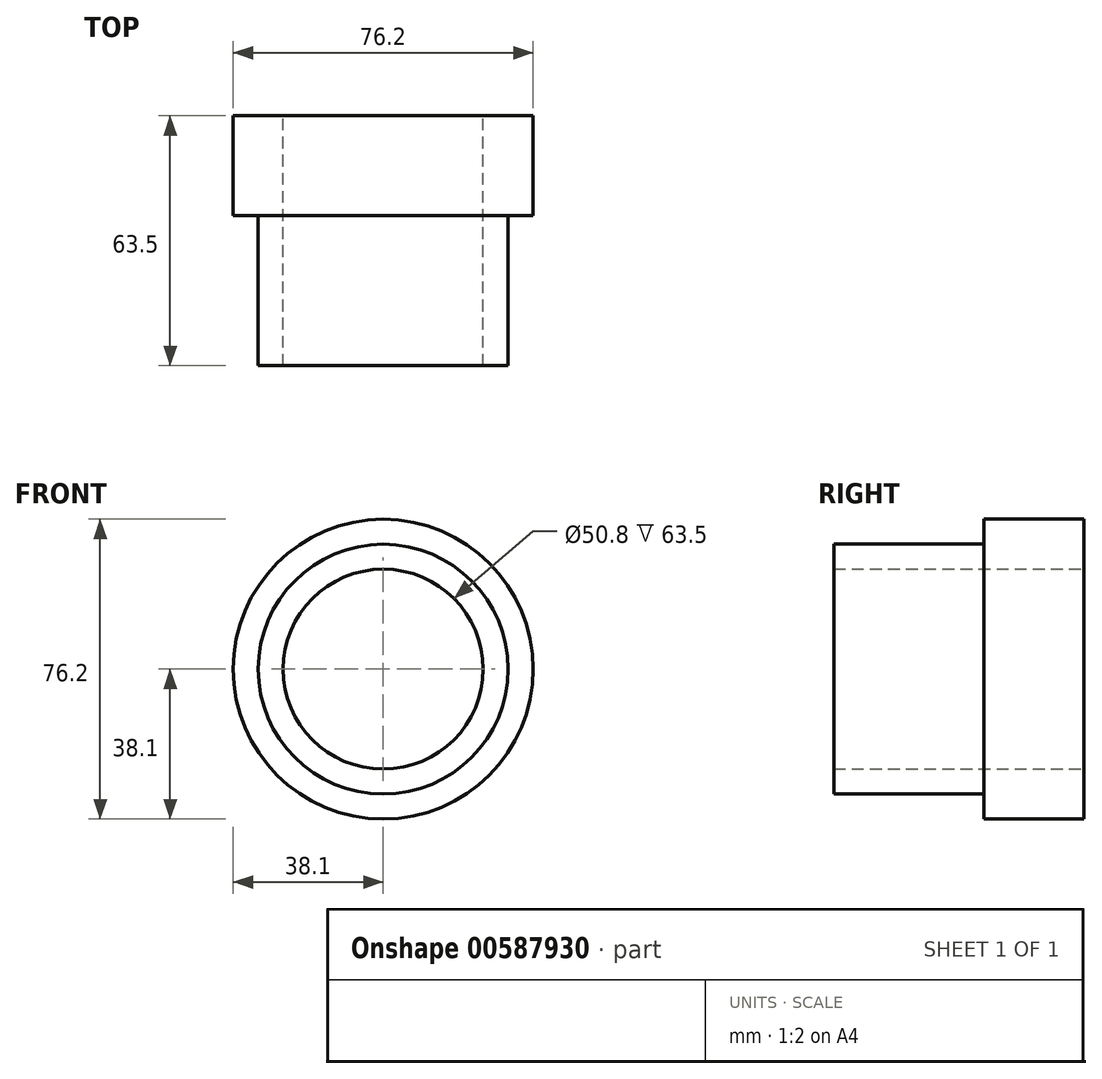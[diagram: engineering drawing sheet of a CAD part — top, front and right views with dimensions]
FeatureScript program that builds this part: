
annotation { "Feature Type Name" : "Feature", "Feature Type Description" : "" }
export const myFeature = defineFeature(function(context is Context, id is Id, definition is map)
    precondition{}
    {
        {
            var Q0;
            Q0=qCreatedBy(makeId("Front.planeOp"),FACE);
            var sketch = newSketch(context, id + "F0", { "sketchPlane" : qUnion([Q0])});
            skCircle(sketch, "E0", {"center": v(0, 0) * mm, "radius": 31.75 * mm});
            skCircle(sketch, "E1.0", {"center": v(0, 0) * mm, "radius": 25.4 * mm});
            skSolve(sketch);
        }
        {
            var Q0;
            Q0 = qSketchRegion(id + "F0", true);
            extrude(context, id + "F1", {"entities" : qUnion([Q0]), "depth" : 38.1 * mm, "offsetDistance" : 25.4 * mm});
        }
        {
            var Q0;
            Q0=qCreatedBy(makeId("Front.planeOp"),FACE);
            var sketch = newSketch(context, id + "F2", { "sketchPlane" : qUnion([Q0])});
            skCircle(sketch, "E2", {"center": v(0, 0) * mm, "radius": 38.1 * mm});
            skCircle(sketch, "E3", {"center": v(0, 0) * mm, "radius": 25.4 * mm});
            skSolve(sketch);
        }
        {
            var Q0;
            Q0 = qSketchRegion(id + "F2", true);
            extrude(context, id + "F3", {"entities" : qUnion([Q0]), "operationType" : NewBodyOperationType.ADD, "oppositeDirection" : true, "depth" : 25.4 * mm, "offsetDistance" : 25.4 * mm});
        }
    });
